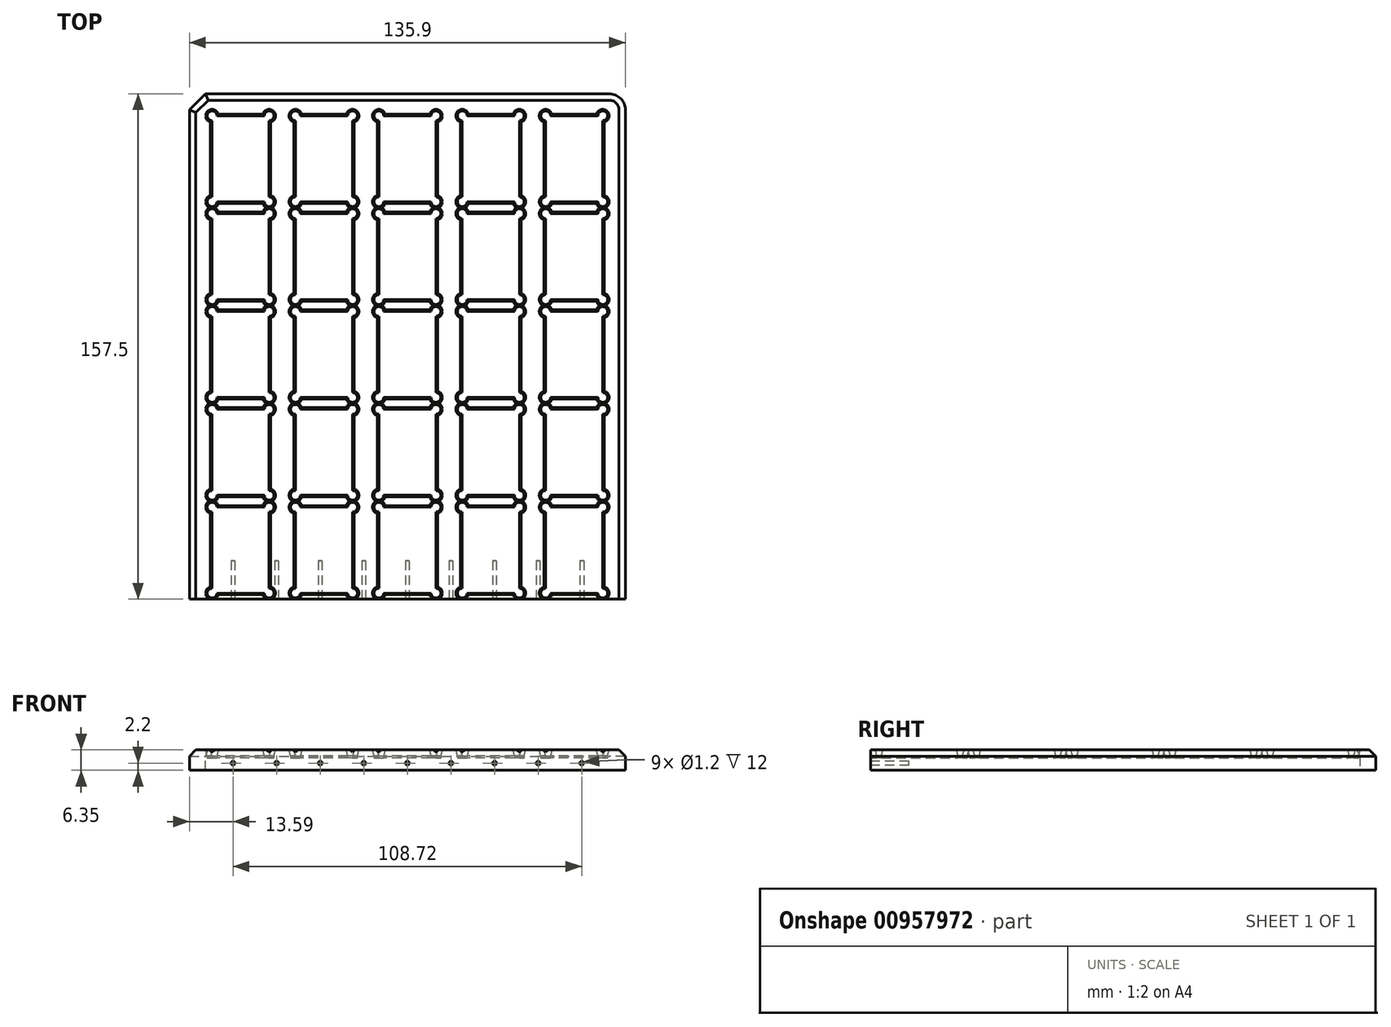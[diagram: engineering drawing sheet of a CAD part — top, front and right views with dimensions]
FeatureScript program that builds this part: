
annotation { "Feature Type Name" : "Feature", "Feature Type Description" : "" }
export const myFeature = defineFeature(function(context is Context, id is Id, definition is map)
    precondition{}
    {
        {
            var Q0;
            Q0=qCreatedBy(makeId("Top.planeOp"),FACE);
            var sketch = newSketch(context, id + "F0", { "sketchPlane" : qUnion([Q0])});
            skLineSegment(sketch, "E0.bottom", {"start": v(0, 0) * mm, "end": v(135.9, 0) * mm});
            skLineSegment(sketch, "E0.top", {"start": v(0, -157.5) * mm, "end": v(135.9, -157.5) * mm});
            skLineSegment(sketch, "E0.left", {"start": v(0, 0) * mm, "end": v(0, -157.5) * mm});
            skLineSegment(sketch, "E0.right", {"start": v(135.9, 0) * mm, "end": v(135.9, -157.5) * mm});
            skSolve(sketch);
        }
        {
            var Q0;
            Q0=makeQuery(id+"F0.imprint","IMPRINT",FACE,{"disambiguationData":[TD([[makeQuery(id+"F0.imprint","IMPRINT",EDGE,{"derivedFrom":sQuery(id+"F0.wireOp",EDGE,"E0.bottom")}),-1.0]])]});
            extrude(context, id + "F1", {"entities" : qUnion([Q0]), "depth" : 3.85 * mm, "offsetDistance" : 25 * mm});
        }
        {
            var Q0;
            Q0=makeQuery(id+"F1.opExtrude","SWEPT_EDGE",EDGE,{"disambiguationData":[OSD([sQuery(id+"F0.wireOp",EDGE,"E0.bottom"),sQuery(id+"F0.wireOp",EDGE,"E0.left")])]});
            chamfer(context, id + "F2", {"entities" : qUnion([Q0]), "chamferType" : ChamferType.OFFSET_ANGLE, "width" : 5 * mm, "oppositeDirection" : false, "angle" : 45 * degree, "tangentPropagation" : true});
        }
        {
            var Q0;
            {var subQ0=sQuery(id+"F0.wireOp",EDGE,"E0.right");var subQ1=sQuery(id+"F0.wireOp",EDGE,"E0.bottom");Q0=makeQuery(id+"F5.boolean.opBoolean","MERGE",EDGE,{"derivedFrom":[makeQuery(id+"F1.opExtrude","SWEPT_EDGE",EDGE,{"disambiguationData":[OSD([subQ1,subQ0])]}),makeQuery(id+"F5.opExtrude","SWEPT_EDGE",EDGE,{"disambiguationData":[OSD([subQ1,subQ0])]})]});}
            fillet(context, id + "F3", {"entities" : qUnion([Q0]), "radius" : 5 * mm, "tangentPropagation" : true, "allowEdgeOverflow" : false});
        }
        {
            var Q0;
            Q0=makeQuery(id+"F1.opExtrude","CAP_FACE",FACE,{"disambiguationData":[OSD([sQuery(id+"F0.wireOp",EDGE,"E0.bottom"),sQuery(id+"F0.wireOp",EDGE,"E0.top"),sQuery(id+"F0.wireOp",EDGE,"E0.left"),sQuery(id+"F0.wireOp",EDGE,"E0.right")])],"isStart":false});
            var sketch = newSketch(context, id + "F4", { "sketchPlane" : qUnion([Q0])});
            skLineSegment(sketch, "E1.bottom", {"start": v(24.85, -33.65) * mm, "end": v(7.05, -33.65) * mm});
            skLineSegment(sketch, "E1.top", {"start": v(24.85, -6.85) * mm, "end": v(7.05, -6.85) * mm});
            skLineSegment(sketch, "E1.left", {"start": v(24.85, -33.65) * mm, "end": v(24.85, -6.85) * mm});
            skLineSegment(sketch, "E1.right", {"start": v(7.05, -33.65) * mm, "end": v(7.05, -6.85) * mm});
            skPoint(sketch, "E1.middle", {"position": v(15.95, -20.25) * mm});
            skCircle(sketch, "E2", {"center": v(7.05, -6.85) * mm, "radius": 1.5 * mm});
            skCircle(sketch, "E3", {"center": v(24.85, -6.85) * mm, "radius": 1.5 * mm});
            skCircle(sketch, "E4", {"center": v(24.85, -33.65) * mm, "radius": 1.5 * mm});
            skCircle(sketch, "E5", {"center": v(7.05, -33.65) * mm, "radius": 1.5 * mm});
            skLineSegment(sketch, "E6.0.1.0", {"start": v(24.85, -64.15) * mm, "end": v(7.05, -64.15) * mm});
            skCircle(sketch, "E6.0.1.1", {"center": v(7.05, -64.15) * mm, "radius": 1.5 * mm});
            skLineSegment(sketch, "E6.0.1.2", {"start": v(7.05, -64.15) * mm, "end": v(7.05, -37.35) * mm});
            skCircle(sketch, "E6.0.1.3", {"center": v(7.05, -37.35) * mm, "radius": 1.5 * mm});
            skLineSegment(sketch, "E6.0.1.4", {"start": v(24.85, -37.35) * mm, "end": v(7.05, -37.35) * mm});
            skCircle(sketch, "E6.0.1.5", {"center": v(24.85, -37.35) * mm, "radius": 1.5 * mm});
            skLineSegment(sketch, "E6.0.1.6", {"start": v(24.85, -64.15) * mm, "end": v(24.85, -37.35) * mm});
            skCircle(sketch, "E6.0.1.7", {"center": v(24.85, -64.15) * mm, "radius": 1.5 * mm});
            skLineSegment(sketch, "E6.0.2.0", {"start": v(24.85, -94.65) * mm, "end": v(7.05, -94.65) * mm});
            skCircle(sketch, "E6.0.2.1", {"center": v(7.05, -94.65) * mm, "radius": 1.5 * mm});
            skLineSegment(sketch, "E6.0.2.2", {"start": v(7.05, -94.65) * mm, "end": v(7.05, -67.85) * mm});
            skCircle(sketch, "E6.0.2.3", {"center": v(7.05, -67.85) * mm, "radius": 1.5 * mm});
            skLineSegment(sketch, "E6.0.2.4", {"start": v(24.85, -67.85) * mm, "end": v(7.05, -67.85) * mm});
            skCircle(sketch, "E6.0.2.5", {"center": v(24.85, -67.85) * mm, "radius": 1.5 * mm});
            skLineSegment(sketch, "E6.0.2.6", {"start": v(24.85, -94.65) * mm, "end": v(24.85, -67.85) * mm});
            skCircle(sketch, "E6.0.2.7", {"center": v(24.85, -94.65) * mm, "radius": 1.5 * mm});
            skLineSegment(sketch, "E6.0.3.0", {"start": v(24.85, -125.15) * mm, "end": v(7.05, -125.15) * mm});
            skCircle(sketch, "E6.0.3.1", {"center": v(7.05, -125.15) * mm, "radius": 1.5 * mm});
            skLineSegment(sketch, "E6.0.3.2", {"start": v(7.05, -125.15) * mm, "end": v(7.05, -98.35) * mm});
            skCircle(sketch, "E6.0.3.3", {"center": v(7.05, -98.35) * mm, "radius": 1.5 * mm});
            skLineSegment(sketch, "E6.0.3.4", {"start": v(24.85, -98.35) * mm, "end": v(7.05, -98.35) * mm});
            skCircle(sketch, "E6.0.3.5", {"center": v(24.85, -98.35) * mm, "radius": 1.5 * mm});
            skLineSegment(sketch, "E6.0.3.6", {"start": v(24.85, -125.15) * mm, "end": v(24.85, -98.35) * mm});
            skCircle(sketch, "E6.0.3.7", {"center": v(24.85, -125.15) * mm, "radius": 1.5 * mm});
            skLineSegment(sketch, "E6.0.4.0", {"start": v(24.85, -155.65) * mm, "end": v(7.05, -155.65) * mm});
            skCircle(sketch, "E6.0.4.1", {"center": v(7.05, -155.65) * mm, "radius": 1.5 * mm});
            skLineSegment(sketch, "E6.0.4.2", {"start": v(7.05, -155.65) * mm, "end": v(7.05, -128.85) * mm});
            skCircle(sketch, "E6.0.4.3", {"center": v(7.05, -128.85) * mm, "radius": 1.5 * mm});
            skLineSegment(sketch, "E6.0.4.4", {"start": v(24.85, -128.85) * mm, "end": v(7.05, -128.85) * mm});
            skCircle(sketch, "E6.0.4.5", {"center": v(24.85, -128.85) * mm, "radius": 1.5 * mm});
            skLineSegment(sketch, "E6.0.4.6", {"start": v(24.85, -155.65) * mm, "end": v(24.85, -128.85) * mm});
            skCircle(sketch, "E6.0.4.7", {"center": v(24.85, -155.65) * mm, "radius": 1.5 * mm});
            skLineSegment(sketch, "E6.1.0.0", {"start": v(50.85, -33.65) * mm, "end": v(33.05, -33.65) * mm});
            skCircle(sketch, "E6.1.0.1", {"center": v(33.05, -33.65) * mm, "radius": 1.5 * mm});
            skLineSegment(sketch, "E6.1.0.2", {"start": v(33.05, -33.65) * mm, "end": v(33.05, -6.85) * mm});
            skCircle(sketch, "E6.1.0.3", {"center": v(33.05, -6.85) * mm, "radius": 1.5 * mm});
            skLineSegment(sketch, "E6.1.0.4", {"start": v(50.85, -6.85) * mm, "end": v(33.05, -6.85) * mm});
            skCircle(sketch, "E6.1.0.5", {"center": v(50.85, -6.85) * mm, "radius": 1.5 * mm});
            skLineSegment(sketch, "E6.1.0.6", {"start": v(50.85, -33.65) * mm, "end": v(50.85, -6.85) * mm});
            skCircle(sketch, "E6.1.0.7", {"center": v(50.85, -33.65) * mm, "radius": 1.5 * mm});
            skLineSegment(sketch, "E6.1.1.0", {"start": v(50.85, -64.15) * mm, "end": v(33.05, -64.15) * mm});
            skCircle(sketch, "E6.1.1.1", {"center": v(33.05, -64.15) * mm, "radius": 1.5 * mm});
            skLineSegment(sketch, "E6.1.1.2", {"start": v(33.05, -64.15) * mm, "end": v(33.05, -37.35) * mm});
            skCircle(sketch, "E6.1.1.3", {"center": v(33.05, -37.35) * mm, "radius": 1.5 * mm});
            skLineSegment(sketch, "E6.1.1.4", {"start": v(50.85, -37.35) * mm, "end": v(33.05, -37.35) * mm});
            skCircle(sketch, "E6.1.1.5", {"center": v(50.85, -37.35) * mm, "radius": 1.5 * mm});
            skLineSegment(sketch, "E6.1.1.6", {"start": v(50.85, -64.15) * mm, "end": v(50.85, -37.35) * mm});
            skCircle(sketch, "E6.1.1.7", {"center": v(50.85, -64.15) * mm, "radius": 1.5 * mm});
            skLineSegment(sketch, "E6.1.2.0", {"start": v(50.85, -94.65) * mm, "end": v(33.05, -94.65) * mm});
            skCircle(sketch, "E6.1.2.1", {"center": v(33.05, -94.65) * mm, "radius": 1.5 * mm});
            skLineSegment(sketch, "E6.1.2.2", {"start": v(33.05, -94.65) * mm, "end": v(33.05, -67.85) * mm});
            skCircle(sketch, "E6.1.2.3", {"center": v(33.05, -67.85) * mm, "radius": 1.5 * mm});
            skLineSegment(sketch, "E6.1.2.4", {"start": v(50.85, -67.85) * mm, "end": v(33.05, -67.85) * mm});
            skCircle(sketch, "E6.1.2.5", {"center": v(50.85, -67.85) * mm, "radius": 1.5 * mm});
            skLineSegment(sketch, "E6.1.2.6", {"start": v(50.85, -94.65) * mm, "end": v(50.85, -67.85) * mm});
            skCircle(sketch, "E6.1.2.7", {"center": v(50.85, -94.65) * mm, "radius": 1.5 * mm});
            skLineSegment(sketch, "E6.1.3.0", {"start": v(50.85, -125.15) * mm, "end": v(33.05, -125.15) * mm});
            skCircle(sketch, "E6.1.3.1", {"center": v(33.05, -125.15) * mm, "radius": 1.5 * mm});
            skLineSegment(sketch, "E6.1.3.2", {"start": v(33.05, -125.15) * mm, "end": v(33.05, -98.35) * mm});
            skCircle(sketch, "E6.1.3.3", {"center": v(33.05, -98.35) * mm, "radius": 1.5 * mm});
            skLineSegment(sketch, "E6.1.3.4", {"start": v(50.85, -98.35) * mm, "end": v(33.05, -98.35) * mm});
            skCircle(sketch, "E6.1.3.5", {"center": v(50.85, -98.35) * mm, "radius": 1.5 * mm});
            skLineSegment(sketch, "E6.1.3.6", {"start": v(50.85, -125.15) * mm, "end": v(50.85, -98.35) * mm});
            skCircle(sketch, "E6.1.3.7", {"center": v(50.85, -125.15) * mm, "radius": 1.5 * mm});
            skLineSegment(sketch, "E6.1.4.0", {"start": v(50.85, -155.65) * mm, "end": v(33.05, -155.65) * mm});
            skCircle(sketch, "E6.1.4.1", {"center": v(33.05, -155.65) * mm, "radius": 1.5 * mm});
            skLineSegment(sketch, "E6.1.4.2", {"start": v(33.05, -155.65) * mm, "end": v(33.05, -128.85) * mm});
            skCircle(sketch, "E6.1.4.3", {"center": v(33.05, -128.85) * mm, "radius": 1.5 * mm});
            skLineSegment(sketch, "E6.1.4.4", {"start": v(50.85, -128.85) * mm, "end": v(33.05, -128.85) * mm});
            skCircle(sketch, "E6.1.4.5", {"center": v(50.85, -128.85) * mm, "radius": 1.5 * mm});
            skLineSegment(sketch, "E6.1.4.6", {"start": v(50.85, -155.65) * mm, "end": v(50.85, -128.85) * mm});
            skCircle(sketch, "E6.1.4.7", {"center": v(50.85, -155.65) * mm, "radius": 1.5 * mm});
            skLineSegment(sketch, "E6.2.0.0", {"start": v(76.85, -33.65) * mm, "end": v(59.05, -33.65) * mm});
            skCircle(sketch, "E6.2.0.1", {"center": v(59.05, -33.65) * mm, "radius": 1.5 * mm});
            skLineSegment(sketch, "E6.2.0.2", {"start": v(59.05, -33.65) * mm, "end": v(59.05, -6.85) * mm});
            skCircle(sketch, "E6.2.0.3", {"center": v(59.05, -6.85) * mm, "radius": 1.5 * mm});
            skLineSegment(sketch, "E6.2.0.4", {"start": v(76.85, -6.85) * mm, "end": v(59.05, -6.85) * mm});
            skCircle(sketch, "E6.2.0.5", {"center": v(76.85, -6.85) * mm, "radius": 1.5 * mm});
            skLineSegment(sketch, "E6.2.0.6", {"start": v(76.85, -33.65) * mm, "end": v(76.85, -6.85) * mm});
            skCircle(sketch, "E6.2.0.7", {"center": v(76.85, -33.65) * mm, "radius": 1.5 * mm});
            skLineSegment(sketch, "E6.2.1.0", {"start": v(76.85, -64.15) * mm, "end": v(59.05, -64.15) * mm});
            skCircle(sketch, "E6.2.1.1", {"center": v(59.05, -64.15) * mm, "radius": 1.5 * mm});
            skLineSegment(sketch, "E6.2.1.2", {"start": v(59.05, -64.15) * mm, "end": v(59.05, -37.35) * mm});
            skCircle(sketch, "E6.2.1.3", {"center": v(59.05, -37.35) * mm, "radius": 1.5 * mm});
            skLineSegment(sketch, "E6.2.1.4", {"start": v(76.85, -37.35) * mm, "end": v(59.05, -37.35) * mm});
            skCircle(sketch, "E6.2.1.5", {"center": v(76.85, -37.35) * mm, "radius": 1.5 * mm});
            skLineSegment(sketch, "E6.2.1.6", {"start": v(76.85, -64.15) * mm, "end": v(76.85, -37.35) * mm});
            skCircle(sketch, "E6.2.1.7", {"center": v(76.85, -64.15) * mm, "radius": 1.5 * mm});
            skLineSegment(sketch, "E6.2.2.0", {"start": v(76.85, -94.65) * mm, "end": v(59.05, -94.65) * mm});
            skCircle(sketch, "E6.2.2.1", {"center": v(59.05, -94.65) * mm, "radius": 1.5 * mm});
            skLineSegment(sketch, "E6.2.2.2", {"start": v(59.05, -94.65) * mm, "end": v(59.05, -67.85) * mm});
            skCircle(sketch, "E6.2.2.3", {"center": v(59.05, -67.85) * mm, "radius": 1.5 * mm});
            skLineSegment(sketch, "E6.2.2.4", {"start": v(76.85, -67.85) * mm, "end": v(59.05, -67.85) * mm});
            skCircle(sketch, "E6.2.2.5", {"center": v(76.85, -67.85) * mm, "radius": 1.5 * mm});
            skLineSegment(sketch, "E6.2.2.6", {"start": v(76.85, -94.65) * mm, "end": v(76.85, -67.85) * mm});
            skCircle(sketch, "E6.2.2.7", {"center": v(76.85, -94.65) * mm, "radius": 1.5 * mm});
            skLineSegment(sketch, "E6.2.3.0", {"start": v(76.85, -125.15) * mm, "end": v(59.05, -125.15) * mm});
            skCircle(sketch, "E6.2.3.1", {"center": v(59.05, -125.15) * mm, "radius": 1.5 * mm});
            skLineSegment(sketch, "E6.2.3.2", {"start": v(59.05, -125.15) * mm, "end": v(59.05, -98.35) * mm});
            skCircle(sketch, "E6.2.3.3", {"center": v(59.05, -98.35) * mm, "radius": 1.5 * mm});
            skLineSegment(sketch, "E6.2.3.4", {"start": v(76.85, -98.35) * mm, "end": v(59.05, -98.35) * mm});
            skCircle(sketch, "E6.2.3.5", {"center": v(76.85, -98.35) * mm, "radius": 1.5 * mm});
            skLineSegment(sketch, "E6.2.3.6", {"start": v(76.85, -125.15) * mm, "end": v(76.85, -98.35) * mm});
            skCircle(sketch, "E6.2.3.7", {"center": v(76.85, -125.15) * mm, "radius": 1.5 * mm});
            skLineSegment(sketch, "E6.2.4.0", {"start": v(76.85, -155.65) * mm, "end": v(59.05, -155.65) * mm});
            skCircle(sketch, "E6.2.4.1", {"center": v(59.05, -155.65) * mm, "radius": 1.5 * mm});
            skLineSegment(sketch, "E6.2.4.2", {"start": v(59.05, -155.65) * mm, "end": v(59.05, -128.85) * mm});
            skCircle(sketch, "E6.2.4.3", {"center": v(59.05, -128.85) * mm, "radius": 1.5 * mm});
            skLineSegment(sketch, "E6.2.4.4", {"start": v(76.85, -128.85) * mm, "end": v(59.05, -128.85) * mm});
            skCircle(sketch, "E6.2.4.5", {"center": v(76.85, -128.85) * mm, "radius": 1.5 * mm});
            skLineSegment(sketch, "E6.2.4.6", {"start": v(76.85, -155.65) * mm, "end": v(76.85, -128.85) * mm});
            skCircle(sketch, "E6.2.4.7", {"center": v(76.85, -155.65) * mm, "radius": 1.5 * mm});
            skLineSegment(sketch, "E6.3.0.0", {"start": v(102.85, -33.65) * mm, "end": v(85.05, -33.65) * mm});
            skCircle(sketch, "E6.3.0.1", {"center": v(85.05, -33.65) * mm, "radius": 1.5 * mm});
            skLineSegment(sketch, "E6.3.0.2", {"start": v(85.05, -33.65) * mm, "end": v(85.05, -6.85) * mm});
            skCircle(sketch, "E6.3.0.3", {"center": v(85.05, -6.85) * mm, "radius": 1.5 * mm});
            skLineSegment(sketch, "E6.3.0.4", {"start": v(102.85, -6.85) * mm, "end": v(85.05, -6.85) * mm});
            skCircle(sketch, "E6.3.0.5", {"center": v(102.85, -6.85) * mm, "radius": 1.5 * mm});
            skLineSegment(sketch, "E6.3.0.6", {"start": v(102.85, -33.65) * mm, "end": v(102.85, -6.85) * mm});
            skCircle(sketch, "E6.3.0.7", {"center": v(102.85, -33.65) * mm, "radius": 1.5 * mm});
            skLineSegment(sketch, "E6.3.1.0", {"start": v(102.85, -64.15) * mm, "end": v(85.05, -64.15) * mm});
            skCircle(sketch, "E6.3.1.1", {"center": v(85.05, -64.15) * mm, "radius": 1.5 * mm});
            skLineSegment(sketch, "E6.3.1.2", {"start": v(85.05, -64.15) * mm, "end": v(85.05, -37.35) * mm});
            skCircle(sketch, "E6.3.1.3", {"center": v(85.05, -37.35) * mm, "radius": 1.5 * mm});
            skLineSegment(sketch, "E6.3.1.4", {"start": v(102.85, -37.35) * mm, "end": v(85.05, -37.35) * mm});
            skCircle(sketch, "E6.3.1.5", {"center": v(102.85, -37.35) * mm, "radius": 1.5 * mm});
            skLineSegment(sketch, "E6.3.1.6", {"start": v(102.85, -64.15) * mm, "end": v(102.85, -37.35) * mm});
            skCircle(sketch, "E6.3.1.7", {"center": v(102.85, -64.15) * mm, "radius": 1.5 * mm});
            skLineSegment(sketch, "E6.3.2.0", {"start": v(102.85, -94.65) * mm, "end": v(85.05, -94.65) * mm});
            skCircle(sketch, "E6.3.2.1", {"center": v(85.05, -94.65) * mm, "radius": 1.5 * mm});
            skLineSegment(sketch, "E6.3.2.2", {"start": v(85.05, -94.65) * mm, "end": v(85.05, -67.85) * mm});
            skCircle(sketch, "E6.3.2.3", {"center": v(85.05, -67.85) * mm, "radius": 1.5 * mm});
            skLineSegment(sketch, "E6.3.2.4", {"start": v(102.85, -67.85) * mm, "end": v(85.05, -67.85) * mm});
            skCircle(sketch, "E6.3.2.5", {"center": v(102.85, -67.85) * mm, "radius": 1.5 * mm});
            skLineSegment(sketch, "E6.3.2.6", {"start": v(102.85, -94.65) * mm, "end": v(102.85, -67.85) * mm});
            skCircle(sketch, "E6.3.2.7", {"center": v(102.85, -94.65) * mm, "radius": 1.5 * mm});
            skLineSegment(sketch, "E6.3.3.0", {"start": v(102.85, -125.15) * mm, "end": v(85.05, -125.15) * mm});
            skCircle(sketch, "E6.3.3.1", {"center": v(85.05, -125.15) * mm, "radius": 1.5 * mm});
            skLineSegment(sketch, "E6.3.3.2", {"start": v(85.05, -125.15) * mm, "end": v(85.05, -98.35) * mm});
            skCircle(sketch, "E6.3.3.3", {"center": v(85.05, -98.35) * mm, "radius": 1.5 * mm});
            skLineSegment(sketch, "E6.3.3.4", {"start": v(102.85, -98.35) * mm, "end": v(85.05, -98.35) * mm});
            skCircle(sketch, "E6.3.3.5", {"center": v(102.85, -98.35) * mm, "radius": 1.5 * mm});
            skLineSegment(sketch, "E6.3.3.6", {"start": v(102.85, -125.15) * mm, "end": v(102.85, -98.35) * mm});
            skCircle(sketch, "E6.3.3.7", {"center": v(102.85, -125.15) * mm, "radius": 1.5 * mm});
            skLineSegment(sketch, "E6.3.4.0", {"start": v(102.85, -155.65) * mm, "end": v(85.05, -155.65) * mm});
            skCircle(sketch, "E6.3.4.1", {"center": v(85.05, -155.65) * mm, "radius": 1.5 * mm});
            skLineSegment(sketch, "E6.3.4.2", {"start": v(85.05, -155.65) * mm, "end": v(85.05, -128.85) * mm});
            skCircle(sketch, "E6.3.4.3", {"center": v(85.05, -128.85) * mm, "radius": 1.5 * mm});
            skLineSegment(sketch, "E6.3.4.4", {"start": v(102.85, -128.85) * mm, "end": v(85.05, -128.85) * mm});
            skCircle(sketch, "E6.3.4.5", {"center": v(102.85, -128.85) * mm, "radius": 1.5 * mm});
            skLineSegment(sketch, "E6.3.4.6", {"start": v(102.85, -155.65) * mm, "end": v(102.85, -128.85) * mm});
            skCircle(sketch, "E6.3.4.7", {"center": v(102.85, -155.65) * mm, "radius": 1.5 * mm});
            skLineSegment(sketch, "E6.4.0.0", {"start": v(128.85, -33.65) * mm, "end": v(111.05, -33.65) * mm});
            skCircle(sketch, "E6.4.0.1", {"center": v(111.05, -33.65) * mm, "radius": 1.5 * mm});
            skLineSegment(sketch, "E6.4.0.2", {"start": v(111.05, -33.65) * mm, "end": v(111.05, -6.85) * mm});
            skCircle(sketch, "E6.4.0.3", {"center": v(111.05, -6.85) * mm, "radius": 1.5 * mm});
            skLineSegment(sketch, "E6.4.0.4", {"start": v(128.85, -6.85) * mm, "end": v(111.05, -6.85) * mm});
            skCircle(sketch, "E6.4.0.5", {"center": v(128.85, -6.85) * mm, "radius": 1.5 * mm});
            skLineSegment(sketch, "E6.4.0.6", {"start": v(128.85, -33.65) * mm, "end": v(128.85, -6.85) * mm});
            skCircle(sketch, "E6.4.0.7", {"center": v(128.85, -33.65) * mm, "radius": 1.5 * mm});
            skLineSegment(sketch, "E6.4.1.0", {"start": v(128.85, -64.15) * mm, "end": v(111.05, -64.15) * mm});
            skCircle(sketch, "E6.4.1.1", {"center": v(111.05, -64.15) * mm, "radius": 1.5 * mm});
            skLineSegment(sketch, "E6.4.1.2", {"start": v(111.05, -64.15) * mm, "end": v(111.05, -37.35) * mm});
            skCircle(sketch, "E6.4.1.3", {"center": v(111.05, -37.35) * mm, "radius": 1.5 * mm});
            skLineSegment(sketch, "E6.4.1.4", {"start": v(128.85, -37.35) * mm, "end": v(111.05, -37.35) * mm});
            skCircle(sketch, "E6.4.1.5", {"center": v(128.85, -37.35) * mm, "radius": 1.5 * mm});
            skLineSegment(sketch, "E6.4.1.6", {"start": v(128.85, -64.15) * mm, "end": v(128.85, -37.35) * mm});
            skCircle(sketch, "E6.4.1.7", {"center": v(128.85, -64.15) * mm, "radius": 1.5 * mm});
            skLineSegment(sketch, "E6.4.2.0", {"start": v(128.85, -94.65) * mm, "end": v(111.05, -94.65) * mm});
            skCircle(sketch, "E6.4.2.1", {"center": v(111.05, -94.65) * mm, "radius": 1.5 * mm});
            skLineSegment(sketch, "E6.4.2.2", {"start": v(111.05, -94.65) * mm, "end": v(111.05, -67.85) * mm});
            skCircle(sketch, "E6.4.2.3", {"center": v(111.05, -67.85) * mm, "radius": 1.5 * mm});
            skLineSegment(sketch, "E6.4.2.4", {"start": v(128.85, -67.85) * mm, "end": v(111.05, -67.85) * mm});
            skCircle(sketch, "E6.4.2.5", {"center": v(128.85, -67.85) * mm, "radius": 1.5 * mm});
            skLineSegment(sketch, "E6.4.2.6", {"start": v(128.85, -94.65) * mm, "end": v(128.85, -67.85) * mm});
            skCircle(sketch, "E6.4.2.7", {"center": v(128.85, -94.65) * mm, "radius": 1.5 * mm});
            skLineSegment(sketch, "E6.4.3.0", {"start": v(128.85, -125.15) * mm, "end": v(111.05, -125.15) * mm});
            skCircle(sketch, "E6.4.3.1", {"center": v(111.05, -125.15) * mm, "radius": 1.5 * mm});
            skLineSegment(sketch, "E6.4.3.2", {"start": v(111.05, -125.15) * mm, "end": v(111.05, -98.35) * mm});
            skCircle(sketch, "E6.4.3.3", {"center": v(111.05, -98.35) * mm, "radius": 1.5 * mm});
            skLineSegment(sketch, "E6.4.3.4", {"start": v(128.85, -98.35) * mm, "end": v(111.05, -98.35) * mm});
            skCircle(sketch, "E6.4.3.5", {"center": v(128.85, -98.35) * mm, "radius": 1.5 * mm});
            skLineSegment(sketch, "E6.4.3.6", {"start": v(128.85, -125.15) * mm, "end": v(128.85, -98.35) * mm});
            skCircle(sketch, "E6.4.3.7", {"center": v(128.85, -125.15) * mm, "radius": 1.5 * mm});
            skLineSegment(sketch, "E6.4.4.0", {"start": v(128.85, -155.65) * mm, "end": v(111.05, -155.65) * mm});
            skCircle(sketch, "E6.4.4.1", {"center": v(111.05, -155.65) * mm, "radius": 1.5 * mm});
            skLineSegment(sketch, "E6.4.4.2", {"start": v(111.05, -155.65) * mm, "end": v(111.05, -128.85) * mm});
            skCircle(sketch, "E6.4.4.3", {"center": v(111.05, -128.85) * mm, "radius": 1.5 * mm});
            skLineSegment(sketch, "E6.4.4.4", {"start": v(128.85, -128.85) * mm, "end": v(111.05, -128.85) * mm});
            skCircle(sketch, "E6.4.4.5", {"center": v(128.85, -128.85) * mm, "radius": 1.5 * mm});
            skLineSegment(sketch, "E6.4.4.6", {"start": v(128.85, -155.65) * mm, "end": v(128.85, -128.85) * mm});
            skCircle(sketch, "E6.4.4.7", {"center": v(128.85, -155.65) * mm, "radius": 1.5 * mm});
            skLineSegment(sketch, "E6.direction1", {"start": v(7.05, -33.65) * mm, "end": v(33.05, -33.65) * mm, "construction": true});
            skLineSegment(sketch, "E6.direction2", {"start": v(7.05, -33.65) * mm, "end": v(7.05, -64.15) * mm, "construction": true});
            skSolve(sketch);
        }
        {
            var Q0;
            {var subQ603=sQuery(id+"F0.wireOp",EDGE,"E0.top");Q0=makeQuery(id+"F4.imprint","IMPRINT",FACE,{"disambiguationData":[TD([[makeQuery(id+"F4.imprint","IMPRINT",EDGE,{"derivedFrom":makeQuery(id+"F1.opExtrude","CAP_EDGE",EDGE,{"disambiguationData":[OSD([subQ603])],"isStart":false})}),1.0]])]});}
            extrude(context, id + "F5", {"entities" : qUnion([Q0]), "operationType" : NewBodyOperationType.ADD, "depth" : 2.5 * mm, "offsetDistance" : 25 * mm});
        }
        {
            var Q0;
            {var subQ0=sQuery(id+"F0.wireOp",EDGE,"E0.top");Q0=makeQuery(id+"F5.boolean.opBoolean","MERGE",FACE,{"derivedFrom":[makeQuery(id+"F1.opExtrude","SWEPT_FACE",FACE,{"disambiguationData":[OSD([subQ0])]}),makeQuery(id+"F5.opExtrude","SWEPT_FACE",FACE,{"disambiguationData":[OSD([subQ0])]})]});}
            var sketch = newSketch(context, id + "F6", { "sketchPlane" : qUnion([Q0])});
            skCircle(sketch, "E7", {"center": v(13.6, 2.2) * mm, "radius": 0.6 * mm});
            skCircle(sketch, "E8.1.0.0", {"center": v(27.18, 2.2) * mm, "radius": 0.6 * mm});
            skCircle(sketch, "E8.2.0.0", {"center": v(40.77, 2.2) * mm, "radius": 0.6 * mm});
            skCircle(sketch, "E8.3.0.0", {"center": v(54.36, 2.2) * mm, "radius": 0.6 * mm});
            skCircle(sketch, "E8.4.0.0", {"center": v(67.95, 2.2) * mm, "radius": 0.6 * mm});
            skCircle(sketch, "E8.5.0.0", {"center": v(81.54, 2.2) * mm, "radius": 0.6 * mm});
            skCircle(sketch, "E8.6.0.0", {"center": v(95.13, 2.2) * mm, "radius": 0.6 * mm});
            skCircle(sketch, "E8.7.0.0", {"center": v(108.72, 2.2) * mm, "radius": 0.6 * mm});
            skCircle(sketch, "E8.8.0.0", {"center": v(122.31, 2.2) * mm, "radius": 0.6 * mm});
            skLineSegment(sketch, "E8.direction1", {"start": v(27.18, 2.2) * mm, "end": v(40.77, 2.2) * mm, "construction": true});
            skSolve(sketch);
        }
        {
            var Q0;
            Q0=makeQuery(id+"F6.imprint","IMPRINT",FACE,{"disambiguationData":[TD([[makeQuery(id+"F6.imprint","IMPRINT",EDGE,{"derivedFrom":sQuery(id+"F6.wireOp",EDGE,"E7")}),1.0]])]});
            var Q1;
            Q1=makeQuery(id+"F6.imprint","IMPRINT",FACE,{"disambiguationData":[TD([[makeQuery(id+"F6.imprint","IMPRINT",EDGE,{"derivedFrom":sQuery(id+"F6.wireOp",EDGE,"E8.1.0.0")}),1.0]])]});
            var Q2;
            Q2=makeQuery(id+"F6.imprint","IMPRINT",FACE,{"disambiguationData":[TD([[makeQuery(id+"F6.imprint","IMPRINT",EDGE,{"derivedFrom":sQuery(id+"F6.wireOp",EDGE,"E8.2.0.0")}),1.0]])]});
            var Q3;
            Q3=makeQuery(id+"F6.imprint","IMPRINT",FACE,{"disambiguationData":[TD([[makeQuery(id+"F6.imprint","IMPRINT",EDGE,{"derivedFrom":sQuery(id+"F6.wireOp",EDGE,"E8.3.0.0")}),1.0]])]});
            var Q4;
            Q4=makeQuery(id+"F6.imprint","IMPRINT",FACE,{"disambiguationData":[TD([[makeQuery(id+"F6.imprint","IMPRINT",EDGE,{"derivedFrom":sQuery(id+"F6.wireOp",EDGE,"E8.4.0.0")}),1.0]])]});
            var Q5;
            Q5=makeQuery(id+"F6.imprint","IMPRINT",FACE,{"disambiguationData":[TD([[makeQuery(id+"F6.imprint","IMPRINT",EDGE,{"derivedFrom":sQuery(id+"F6.wireOp",EDGE,"E8.5.0.0")}),1.0]])]});
            var Q6;
            Q6=makeQuery(id+"F6.imprint","IMPRINT",FACE,{"disambiguationData":[TD([[makeQuery(id+"F6.imprint","IMPRINT",EDGE,{"derivedFrom":sQuery(id+"F6.wireOp",EDGE,"E8.6.0.0")}),1.0]])]});
            var Q7;
            Q7=makeQuery(id+"F6.imprint","IMPRINT",FACE,{"disambiguationData":[TD([[makeQuery(id+"F6.imprint","IMPRINT",EDGE,{"derivedFrom":sQuery(id+"F6.wireOp",EDGE,"E8.7.0.0")}),1.0]])]});
            var Q8;
            Q8=makeQuery(id+"F6.imprint","IMPRINT",FACE,{"disambiguationData":[TD([[makeQuery(id+"F6.imprint","IMPRINT",EDGE,{"derivedFrom":sQuery(id+"F6.wireOp",EDGE,"E8.8.0.0")}),1.0]])]});
            var Q9;
            Q9=sQuery(id+"F6.wireOp",EDGE,"E7");
            var Q10;
            Q10=sQuery(id+"F6.wireOp",EDGE,"E8.1.0.0");
            var Q11;
            Q11=sQuery(id+"F6.wireOp",EDGE,"E8.2.0.0");
            var Q12;
            Q12=sQuery(id+"F6.wireOp",EDGE,"E8.3.0.0");
            var Q13;
            Q13=sQuery(id+"F6.wireOp",EDGE,"E8.4.0.0");
            var Q14;
            Q14=sQuery(id+"F6.wireOp",EDGE,"E8.5.0.0");
            extrude(context, id + "F7", {"entities" : qUnion([Q0, Q1, Q2, Q3, Q4, Q5, Q6, Q7, Q8]), "operationType" : NewBodyOperationType.REMOVE, "surfaceEntities" : qUnion([Q9, Q10, Q11, Q12, Q13, Q14]), "oppositeDirection" : true, "depth" : 12 * mm, "offsetDistance" : 25 * mm});
        }
        {
            var Q0;
            Q0=makeQuery(id+"F5.opExtrude","CAP_EDGE",EDGE,{"disambiguationData":[OSD([sQuery(id+"F4.wireOp",EDGE,"E1.right")])],"isStart":false});
            var Q1;
            Q1=makeQuery(id+"F5.opExtrude","CAP_EDGE",EDGE,{"disambiguationData":[OSD([sQuery(id+"F4.wireOp",EDGE,"E1.left")])],"isStart":false});
            var Q2;
            Q2=makeQuery(id+"F5.opExtrude","CAP_EDGE",EDGE,{"disambiguationData":[OSD([sQuery(id+"F4.wireOp",EDGE,"E6.1.0.2")])],"isStart":false});
            var Q3;
            Q3=makeQuery(id+"F5.opExtrude","CAP_EDGE",EDGE,{"disambiguationData":[OSD([sQuery(id+"F4.wireOp",EDGE,"E6.1.0.6")])],"isStart":false});
            var Q4;
            Q4=makeQuery(id+"F5.opExtrude","CAP_EDGE",EDGE,{"disambiguationData":[OSD([sQuery(id+"F4.wireOp",EDGE,"E6.2.0.2")])],"isStart":false});
            var Q5;
            Q5=makeQuery(id+"F5.opExtrude","CAP_EDGE",EDGE,{"disambiguationData":[OSD([sQuery(id+"F4.wireOp",EDGE,"E6.2.0.6")])],"isStart":false});
            var Q6;
            Q6=makeQuery(id+"F5.opExtrude","CAP_EDGE",EDGE,{"disambiguationData":[OSD([sQuery(id+"F4.wireOp",EDGE,"E6.3.0.2")])],"isStart":false});
            var Q7;
            Q7=makeQuery(id+"F5.opExtrude","CAP_EDGE",EDGE,{"disambiguationData":[OSD([sQuery(id+"F4.wireOp",EDGE,"E6.3.0.6")])],"isStart":false});
            var Q8;
            Q8=makeQuery(id+"F5.opExtrude","CAP_EDGE",EDGE,{"disambiguationData":[OSD([sQuery(id+"F4.wireOp",EDGE,"E6.4.0.2")])],"isStart":false});
            var Q9;
            Q9=makeQuery(id+"F5.opExtrude","CAP_EDGE",EDGE,{"disambiguationData":[OSD([sQuery(id+"F4.wireOp",EDGE,"E6.4.0.6")])],"isStart":false});
            var Q10;
            Q10=makeQuery(id+"F5.opExtrude","CAP_EDGE",EDGE,{"disambiguationData":[OSD([sQuery(id+"F4.wireOp",EDGE,"E1.top")])],"isStart":false});
            var Q11;
            Q11=makeQuery(id+"F5.opExtrude","CAP_EDGE",EDGE,{"disambiguationData":[OSD([sQuery(id+"F4.wireOp",EDGE,"E1.bottom")])],"isStart":false});
            var Q12;
            Q12=makeQuery(id+"F5.opExtrude","CAP_EDGE",EDGE,{"disambiguationData":[OSD([sQuery(id+"F4.wireOp",EDGE,"E6.1.0.0")])],"isStart":false});
            var Q13;
            Q13=makeQuery(id+"F5.opExtrude","CAP_EDGE",EDGE,{"disambiguationData":[OSD([sQuery(id+"F4.wireOp",EDGE,"E6.1.0.4")])],"isStart":false});
            var Q14;
            Q14=makeQuery(id+"F5.opExtrude","CAP_EDGE",EDGE,{"disambiguationData":[OSD([sQuery(id+"F4.wireOp",EDGE,"E6.2.0.0")])],"isStart":false});
            var Q15;
            Q15=makeQuery(id+"F5.opExtrude","CAP_EDGE",EDGE,{"disambiguationData":[OSD([sQuery(id+"F4.wireOp",EDGE,"E6.2.0.4")])],"isStart":false});
            var Q16;
            Q16=makeQuery(id+"F5.opExtrude","CAP_EDGE",EDGE,{"disambiguationData":[OSD([sQuery(id+"F4.wireOp",EDGE,"E6.3.0.4")])],"isStart":false});
            var Q17;
            Q17=makeQuery(id+"F5.opExtrude","CAP_EDGE",EDGE,{"disambiguationData":[OSD([sQuery(id+"F4.wireOp",EDGE,"E6.3.0.0")])],"isStart":false});
            var Q18;
            Q18=makeQuery(id+"F5.opExtrude","CAP_EDGE",EDGE,{"disambiguationData":[OSD([sQuery(id+"F4.wireOp",EDGE,"E6.4.0.0")])],"isStart":false});
            var Q19;
            Q19=makeQuery(id+"F5.opExtrude","CAP_EDGE",EDGE,{"disambiguationData":[OSD([sQuery(id+"F4.wireOp",EDGE,"E6.4.0.4")])],"isStart":false});
            var Q20;
            Q20=makeQuery(id+"F5.opExtrude","CAP_EDGE",EDGE,{"disambiguationData":[OSD([sQuery(id+"F4.wireOp",EDGE,"E6.4.1.2")])],"isStart":false});
            var Q21;
            Q21=makeQuery(id+"F5.opExtrude","CAP_EDGE",EDGE,{"disambiguationData":[OSD([sQuery(id+"F4.wireOp",EDGE,"E6.4.1.6")])],"isStart":false});
            var Q22;
            Q22=makeQuery(id+"F5.opExtrude","CAP_EDGE",EDGE,{"disambiguationData":[OSD([sQuery(id+"F4.wireOp",EDGE,"E6.4.1.4")])],"isStart":false});
            var Q23;
            Q23=makeQuery(id+"F5.opExtrude","CAP_EDGE",EDGE,{"disambiguationData":[OSD([sQuery(id+"F4.wireOp",EDGE,"E6.4.1.0")])],"isStart":false});
            var Q24;
            Q24=makeQuery(id+"F5.opExtrude","CAP_EDGE",EDGE,{"disambiguationData":[OSD([sQuery(id+"F4.wireOp",EDGE,"E6.3.1.0")])],"isStart":false});
            var Q25;
            Q25=makeQuery(id+"F5.opExtrude","CAP_EDGE",EDGE,{"disambiguationData":[OSD([sQuery(id+"F4.wireOp",EDGE,"E6.3.1.4")])],"isStart":false});
            var Q26;
            Q26=makeQuery(id+"F5.opExtrude","CAP_EDGE",EDGE,{"disambiguationData":[OSD([sQuery(id+"F4.wireOp",EDGE,"E6.3.1.6")])],"isStart":false});
            var Q27;
            Q27=makeQuery(id+"F5.opExtrude","CAP_EDGE",EDGE,{"disambiguationData":[OSD([sQuery(id+"F4.wireOp",EDGE,"E6.3.1.2")])],"isStart":false});
            var Q28;
            Q28=makeQuery(id+"F5.opExtrude","CAP_EDGE",EDGE,{"disambiguationData":[OSD([sQuery(id+"F4.wireOp",EDGE,"E6.2.1.6")])],"isStart":false});
            var Q29;
            Q29=makeQuery(id+"F5.opExtrude","CAP_EDGE",EDGE,{"disambiguationData":[OSD([sQuery(id+"F4.wireOp",EDGE,"E6.2.1.4")])],"isStart":false});
            var Q30;
            Q30=makeQuery(id+"F5.opExtrude","CAP_EDGE",EDGE,{"disambiguationData":[OSD([sQuery(id+"F4.wireOp",EDGE,"E6.2.1.0")])],"isStart":false});
            var Q31;
            Q31=makeQuery(id+"F5.opExtrude","CAP_EDGE",EDGE,{"disambiguationData":[OSD([sQuery(id+"F4.wireOp",EDGE,"E6.2.1.2")])],"isStart":false});
            var Q32;
            Q32=makeQuery(id+"F5.opExtrude","CAP_EDGE",EDGE,{"disambiguationData":[OSD([sQuery(id+"F4.wireOp",EDGE,"E6.1.1.6")])],"isStart":false});
            var Q33;
            Q33=makeQuery(id+"F5.opExtrude","CAP_EDGE",EDGE,{"disambiguationData":[OSD([sQuery(id+"F4.wireOp",EDGE,"E6.1.1.4")])],"isStart":false});
            var Q34;
            Q34=makeQuery(id+"F5.opExtrude","CAP_EDGE",EDGE,{"disambiguationData":[OSD([sQuery(id+"F4.wireOp",EDGE,"E6.1.1.0")])],"isStart":false});
            var Q35;
            Q35=makeQuery(id+"F5.opExtrude","CAP_EDGE",EDGE,{"disambiguationData":[OSD([sQuery(id+"F4.wireOp",EDGE,"E6.1.1.2")])],"isStart":false});
            var Q36;
            Q36=makeQuery(id+"F5.opExtrude","CAP_EDGE",EDGE,{"disambiguationData":[OSD([sQuery(id+"F4.wireOp",EDGE,"E6.0.1.6")])],"isStart":false});
            var Q37;
            Q37=makeQuery(id+"F5.opExtrude","CAP_EDGE",EDGE,{"disambiguationData":[OSD([sQuery(id+"F4.wireOp",EDGE,"E6.0.1.2")])],"isStart":false});
            var Q38;
            Q38=makeQuery(id+"F5.opExtrude","CAP_EDGE",EDGE,{"disambiguationData":[OSD([sQuery(id+"F4.wireOp",EDGE,"E6.0.1.4")])],"isStart":false});
            var Q39;
            Q39=makeQuery(id+"F5.opExtrude","CAP_EDGE",EDGE,{"disambiguationData":[OSD([sQuery(id+"F4.wireOp",EDGE,"E6.0.1.0")])],"isStart":false});
            var Q40;
            Q40=makeQuery(id+"F5.opExtrude","CAP_EDGE",EDGE,{"disambiguationData":[OSD([sQuery(id+"F4.wireOp",EDGE,"E6.0.2.4")])],"isStart":false});
            var Q41;
            Q41=makeQuery(id+"F5.opExtrude","CAP_EDGE",EDGE,{"disambiguationData":[OSD([sQuery(id+"F4.wireOp",EDGE,"E6.0.2.2")])],"isStart":false});
            var Q42;
            Q42=makeQuery(id+"F5.opExtrude","CAP_EDGE",EDGE,{"disambiguationData":[OSD([sQuery(id+"F4.wireOp",EDGE,"E6.0.2.0")])],"isStart":false});
            var Q43;
            Q43=makeQuery(id+"F5.opExtrude","CAP_EDGE",EDGE,{"disambiguationData":[OSD([sQuery(id+"F4.wireOp",EDGE,"E6.0.2.6")])],"isStart":false});
            var Q44;
            Q44=makeQuery(id+"F5.opExtrude","CAP_EDGE",EDGE,{"disambiguationData":[OSD([sQuery(id+"F4.wireOp",EDGE,"E6.1.2.4")])],"isStart":false});
            var Q45;
            Q45=makeQuery(id+"F5.opExtrude","CAP_EDGE",EDGE,{"disambiguationData":[OSD([sQuery(id+"F4.wireOp",EDGE,"E6.1.2.0")])],"isStart":false});
            var Q46;
            Q46=makeQuery(id+"F5.opExtrude","CAP_EDGE",EDGE,{"disambiguationData":[OSD([sQuery(id+"F4.wireOp",EDGE,"E6.1.2.2")])],"isStart":false});
            var Q47;
            Q47=makeQuery(id+"F5.opExtrude","CAP_EDGE",EDGE,{"disambiguationData":[OSD([sQuery(id+"F4.wireOp",EDGE,"E6.1.2.6")])],"isStart":false});
            var Q48;
            Q48=makeQuery(id+"F5.opExtrude","CAP_EDGE",EDGE,{"disambiguationData":[OSD([sQuery(id+"F4.wireOp",EDGE,"E6.2.2.2")])],"isStart":false});
            var Q49;
            Q49=makeQuery(id+"F5.opExtrude","CAP_EDGE",EDGE,{"disambiguationData":[OSD([sQuery(id+"F4.wireOp",EDGE,"E6.2.2.4")])],"isStart":false});
            var Q50;
            Q50=makeQuery(id+"F5.opExtrude","CAP_EDGE",EDGE,{"disambiguationData":[OSD([sQuery(id+"F4.wireOp",EDGE,"E6.2.2.6")])],"isStart":false});
            var Q51;
            Q51=makeQuery(id+"F5.opExtrude","CAP_EDGE",EDGE,{"disambiguationData":[OSD([sQuery(id+"F4.wireOp",EDGE,"E6.2.2.0")])],"isStart":false});
            var Q52;
            Q52=makeQuery(id+"F5.opExtrude","CAP_EDGE",EDGE,{"disambiguationData":[OSD([sQuery(id+"F4.wireOp",EDGE,"E6.3.2.2")])],"isStart":false});
            var Q53;
            Q53=makeQuery(id+"F5.opExtrude","CAP_EDGE",EDGE,{"disambiguationData":[OSD([sQuery(id+"F4.wireOp",EDGE,"E6.3.2.4")])],"isStart":false});
            var Q54;
            Q54=makeQuery(id+"F5.opExtrude","CAP_EDGE",EDGE,{"disambiguationData":[OSD([sQuery(id+"F4.wireOp",EDGE,"E6.3.2.6")])],"isStart":false});
            var Q55;
            Q55=makeQuery(id+"F5.opExtrude","CAP_EDGE",EDGE,{"disambiguationData":[OSD([sQuery(id+"F4.wireOp",EDGE,"E6.3.2.0")])],"isStart":false});
            var Q56;
            Q56=makeQuery(id+"F5.opExtrude","CAP_EDGE",EDGE,{"disambiguationData":[OSD([sQuery(id+"F4.wireOp",EDGE,"E6.4.2.4")])],"isStart":false});
            var Q57;
            Q57=makeQuery(id+"F5.opExtrude","CAP_EDGE",EDGE,{"disambiguationData":[OSD([sQuery(id+"F4.wireOp",EDGE,"E6.4.2.2")])],"isStart":false});
            var Q58;
            Q58=makeQuery(id+"F5.opExtrude","CAP_EDGE",EDGE,{"disambiguationData":[OSD([sQuery(id+"F4.wireOp",EDGE,"E6.4.2.6")])],"isStart":false});
            var Q59;
            Q59=makeQuery(id+"F5.opExtrude","CAP_EDGE",EDGE,{"disambiguationData":[OSD([sQuery(id+"F4.wireOp",EDGE,"E6.4.2.0")])],"isStart":false});
            var Q60;
            Q60=makeQuery(id+"F5.opExtrude","CAP_EDGE",EDGE,{"disambiguationData":[OSD([sQuery(id+"F4.wireOp",EDGE,"E6.0.3.4")])],"isStart":false});
            var Q61;
            Q61=makeQuery(id+"F5.opExtrude","CAP_EDGE",EDGE,{"disambiguationData":[OSD([sQuery(id+"F4.wireOp",EDGE,"E6.0.3.2")])],"isStart":false});
            var Q62;
            Q62=makeQuery(id+"F5.opExtrude","CAP_EDGE",EDGE,{"disambiguationData":[OSD([sQuery(id+"F4.wireOp",EDGE,"E6.0.3.6")])],"isStart":false});
            var Q63;
            Q63=makeQuery(id+"F5.opExtrude","CAP_EDGE",EDGE,{"disambiguationData":[OSD([sQuery(id+"F4.wireOp",EDGE,"E6.1.3.2")])],"isStart":false});
            var Q64;
            Q64=makeQuery(id+"F5.opExtrude","CAP_EDGE",EDGE,{"disambiguationData":[OSD([sQuery(id+"F4.wireOp",EDGE,"E6.1.3.4")])],"isStart":false});
            var Q65;
            Q65=makeQuery(id+"F5.opExtrude","CAP_EDGE",EDGE,{"disambiguationData":[OSD([sQuery(id+"F4.wireOp",EDGE,"E6.1.3.6")])],"isStart":false});
            var Q66;
            Q66=makeQuery(id+"F5.opExtrude","CAP_EDGE",EDGE,{"disambiguationData":[OSD([sQuery(id+"F4.wireOp",EDGE,"E6.2.3.2")])],"isStart":false});
            var Q67;
            Q67=makeQuery(id+"F5.opExtrude","CAP_EDGE",EDGE,{"disambiguationData":[OSD([sQuery(id+"F4.wireOp",EDGE,"E6.2.3.4")])],"isStart":false});
            var Q68;
            Q68=makeQuery(id+"F5.opExtrude","CAP_EDGE",EDGE,{"disambiguationData":[OSD([sQuery(id+"F4.wireOp",EDGE,"E6.2.3.6")])],"isStart":false});
            var Q69;
            Q69=makeQuery(id+"F5.opExtrude","CAP_EDGE",EDGE,{"disambiguationData":[OSD([sQuery(id+"F4.wireOp",EDGE,"E6.3.3.2")])],"isStart":false});
            var Q70;
            Q70=makeQuery(id+"F5.opExtrude","CAP_EDGE",EDGE,{"disambiguationData":[OSD([sQuery(id+"F4.wireOp",EDGE,"E6.3.3.4")])],"isStart":false});
            var Q71;
            Q71=makeQuery(id+"F5.opExtrude","CAP_EDGE",EDGE,{"disambiguationData":[OSD([sQuery(id+"F4.wireOp",EDGE,"E6.3.3.6")])],"isStart":false});
            var Q72;
            Q72=makeQuery(id+"F5.opExtrude","CAP_EDGE",EDGE,{"disambiguationData":[OSD([sQuery(id+"F4.wireOp",EDGE,"E6.4.3.2")])],"isStart":false});
            var Q73;
            Q73=makeQuery(id+"F5.opExtrude","CAP_EDGE",EDGE,{"disambiguationData":[OSD([sQuery(id+"F4.wireOp",EDGE,"E6.4.3.4")])],"isStart":false});
            var Q74;
            Q74=makeQuery(id+"F5.opExtrude","CAP_EDGE",EDGE,{"disambiguationData":[OSD([sQuery(id+"F4.wireOp",EDGE,"E6.4.3.6")])],"isStart":false});
            var Q75;
            Q75=makeQuery(id+"F5.opExtrude","CAP_EDGE",EDGE,{"disambiguationData":[OSD([sQuery(id+"F4.wireOp",EDGE,"E6.0.3.0")])],"isStart":false});
            var Q76;
            Q76=makeQuery(id+"F5.opExtrude","CAP_EDGE",EDGE,{"disambiguationData":[OSD([sQuery(id+"F4.wireOp",EDGE,"E6.1.3.0")])],"isStart":false});
            var Q77;
            Q77=makeQuery(id+"F5.opExtrude","CAP_EDGE",EDGE,{"disambiguationData":[OSD([sQuery(id+"F4.wireOp",EDGE,"E6.2.3.0")])],"isStart":false});
            var Q78;
            Q78=makeQuery(id+"F5.opExtrude","CAP_EDGE",EDGE,{"disambiguationData":[OSD([sQuery(id+"F4.wireOp",EDGE,"E6.3.3.0")])],"isStart":false});
            var Q79;
            Q79=makeQuery(id+"F5.opExtrude","CAP_EDGE",EDGE,{"disambiguationData":[OSD([sQuery(id+"F4.wireOp",EDGE,"E6.4.3.0")])],"isStart":false});
            var Q80;
            Q80=makeQuery(id+"F5.opExtrude","CAP_EDGE",EDGE,{"disambiguationData":[OSD([sQuery(id+"F4.wireOp",EDGE,"E6.4.4.4")])],"isStart":false});
            var Q81;
            Q81=makeQuery(id+"F5.opExtrude","CAP_EDGE",EDGE,{"disambiguationData":[OSD([sQuery(id+"F4.wireOp",EDGE,"E6.4.4.6")])],"isStart":false});
            var Q82;
            Q82=makeQuery(id+"F5.opExtrude","CAP_EDGE",EDGE,{"disambiguationData":[OSD([sQuery(id+"F4.wireOp",EDGE,"E6.4.4.0")])],"isStart":false});
            var Q83;
            Q83=makeQuery(id+"F5.opExtrude","CAP_EDGE",EDGE,{"disambiguationData":[OSD([sQuery(id+"F4.wireOp",EDGE,"E6.4.4.2")])],"isStart":false});
            var Q84;
            Q84=makeQuery(id+"F5.opExtrude","CAP_EDGE",EDGE,{"disambiguationData":[OSD([sQuery(id+"F4.wireOp",EDGE,"E6.3.4.6")])],"isStart":false});
            var Q85;
            Q85=makeQuery(id+"F5.opExtrude","CAP_EDGE",EDGE,{"disambiguationData":[OSD([sQuery(id+"F4.wireOp",EDGE,"E6.3.4.4")])],"isStart":false});
            var Q86;
            Q86=makeQuery(id+"F5.opExtrude","CAP_EDGE",EDGE,{"disambiguationData":[OSD([sQuery(id+"F4.wireOp",EDGE,"E6.3.4.2")])],"isStart":false});
            var Q87;
            Q87=makeQuery(id+"F5.opExtrude","CAP_EDGE",EDGE,{"disambiguationData":[OSD([sQuery(id+"F4.wireOp",EDGE,"E6.3.4.0")])],"isStart":false});
            var Q88;
            Q88=makeQuery(id+"F5.opExtrude","CAP_EDGE",EDGE,{"disambiguationData":[OSD([sQuery(id+"F4.wireOp",EDGE,"E6.2.4.6")])],"isStart":false});
            var Q89;
            Q89=makeQuery(id+"F5.opExtrude","CAP_EDGE",EDGE,{"disambiguationData":[OSD([sQuery(id+"F4.wireOp",EDGE,"E6.2.4.4")])],"isStart":false});
            var Q90;
            Q90=makeQuery(id+"F5.opExtrude","CAP_EDGE",EDGE,{"disambiguationData":[OSD([sQuery(id+"F4.wireOp",EDGE,"E6.2.4.0")])],"isStart":false});
            var Q91;
            Q91=makeQuery(id+"F5.opExtrude","CAP_EDGE",EDGE,{"disambiguationData":[OSD([sQuery(id+"F4.wireOp",EDGE,"E6.2.4.2")])],"isStart":false});
            var Q92;
            Q92=makeQuery(id+"F5.opExtrude","CAP_EDGE",EDGE,{"disambiguationData":[OSD([sQuery(id+"F4.wireOp",EDGE,"E6.1.4.6")])],"isStart":false});
            var Q93;
            Q93=makeQuery(id+"F5.opExtrude","CAP_EDGE",EDGE,{"disambiguationData":[OSD([sQuery(id+"F4.wireOp",EDGE,"E6.1.4.4")])],"isStart":false});
            var Q94;
            Q94=makeQuery(id+"F5.opExtrude","CAP_EDGE",EDGE,{"disambiguationData":[OSD([sQuery(id+"F4.wireOp",EDGE,"E6.1.4.2")])],"isStart":false});
            var Q95;
            Q95=makeQuery(id+"F5.opExtrude","CAP_EDGE",EDGE,{"disambiguationData":[OSD([sQuery(id+"F4.wireOp",EDGE,"E6.1.4.0")])],"isStart":false});
            var Q96;
            Q96=makeQuery(id+"F5.opExtrude","CAP_EDGE",EDGE,{"disambiguationData":[OSD([sQuery(id+"F4.wireOp",EDGE,"E6.0.4.6")])],"isStart":false});
            var Q97;
            Q97=makeQuery(id+"F5.opExtrude","CAP_EDGE",EDGE,{"disambiguationData":[OSD([sQuery(id+"F4.wireOp",EDGE,"E6.0.4.4")])],"isStart":false});
            var Q98;
            Q98=makeQuery(id+"F5.opExtrude","CAP_EDGE",EDGE,{"disambiguationData":[OSD([sQuery(id+"F4.wireOp",EDGE,"E6.0.4.2")])],"isStart":false});
            var Q99;
            Q99=makeQuery(id+"F5.opExtrude","CAP_EDGE",EDGE,{"disambiguationData":[OSD([sQuery(id+"F4.wireOp",EDGE,"E6.0.4.0")])],"isStart":false});
            var Q100;
            Q100=makeQuery(id+"F5.opExtrude","CAP_EDGE",EDGE,{"disambiguationData":[OSD([sQuery(id+"F4.wireOp",EDGE,"E2")])],"isStart":false});
            var Q101;
            Q101=makeQuery(id+"F5.opExtrude","CAP_EDGE",EDGE,{"disambiguationData":[OSD([sQuery(id+"F4.wireOp",EDGE,"E3")])],"isStart":false});
            var Q102;
            Q102=makeQuery(id+"F5.opExtrude","CAP_EDGE",EDGE,{"disambiguationData":[OSD([sQuery(id+"F4.wireOp",EDGE,"E4")])],"isStart":false});
            var Q103;
            Q103=makeQuery(id+"F5.opExtrude","CAP_EDGE",EDGE,{"disambiguationData":[OSD([sQuery(id+"F4.wireOp",EDGE,"E5")])],"isStart":false});
            var Q104;
            Q104=makeQuery(id+"F5.opExtrude","CAP_EDGE",EDGE,{"disambiguationData":[OSD([sQuery(id+"F4.wireOp",EDGE,"E6.1.0.1")])],"isStart":false});
            var Q105;
            Q105=makeQuery(id+"F5.opExtrude","CAP_EDGE",EDGE,{"disambiguationData":[OSD([sQuery(id+"F4.wireOp",EDGE,"E6.1.0.3")])],"isStart":false});
            var Q106;
            Q106=makeQuery(id+"F5.opExtrude","CAP_EDGE",EDGE,{"disambiguationData":[OSD([sQuery(id+"F4.wireOp",EDGE,"E6.1.0.5")])],"isStart":false});
            var Q107;
            Q107=makeQuery(id+"F5.opExtrude","CAP_EDGE",EDGE,{"disambiguationData":[OSD([sQuery(id+"F4.wireOp",EDGE,"E6.1.0.7")])],"isStart":false});
            var Q108;
            Q108=makeQuery(id+"F5.opExtrude","CAP_EDGE",EDGE,{"disambiguationData":[OSD([sQuery(id+"F4.wireOp",EDGE,"E6.2.0.1")])],"isStart":false});
            var Q109;
            Q109=makeQuery(id+"F5.opExtrude","CAP_EDGE",EDGE,{"disambiguationData":[OSD([sQuery(id+"F4.wireOp",EDGE,"E6.2.0.3")])],"isStart":false});
            var Q110;
            Q110=makeQuery(id+"F5.opExtrude","CAP_EDGE",EDGE,{"disambiguationData":[OSD([sQuery(id+"F4.wireOp",EDGE,"E6.2.0.5")])],"isStart":false});
            var Q111;
            Q111=makeQuery(id+"F5.opExtrude","CAP_EDGE",EDGE,{"disambiguationData":[OSD([sQuery(id+"F4.wireOp",EDGE,"E6.2.0.7")])],"isStart":false});
            var Q112;
            Q112=makeQuery(id+"F5.opExtrude","CAP_EDGE",EDGE,{"disambiguationData":[OSD([sQuery(id+"F4.wireOp",EDGE,"E6.3.0.3")])],"isStart":false});
            var Q113;
            Q113=makeQuery(id+"F5.opExtrude","CAP_EDGE",EDGE,{"disambiguationData":[OSD([sQuery(id+"F4.wireOp",EDGE,"E6.3.0.1")])],"isStart":false});
            var Q114;
            Q114=makeQuery(id+"F5.opExtrude","CAP_EDGE",EDGE,{"disambiguationData":[OSD([sQuery(id+"F4.wireOp",EDGE,"E6.3.0.7")])],"isStart":false});
            var Q115;
            Q115=makeQuery(id+"F5.opExtrude","CAP_EDGE",EDGE,{"disambiguationData":[OSD([sQuery(id+"F4.wireOp",EDGE,"E6.3.0.5")])],"isStart":false});
            var Q116;
            Q116=makeQuery(id+"F5.opExtrude","CAP_EDGE",EDGE,{"disambiguationData":[OSD([sQuery(id+"F4.wireOp",EDGE,"E6.4.0.3")])],"isStart":false});
            var Q117;
            Q117=makeQuery(id+"F5.opExtrude","CAP_EDGE",EDGE,{"disambiguationData":[OSD([sQuery(id+"F4.wireOp",EDGE,"E6.4.0.5")])],"isStart":false});
            var Q118;
            Q118=makeQuery(id+"F5.opExtrude","CAP_EDGE",EDGE,{"disambiguationData":[OSD([sQuery(id+"F4.wireOp",EDGE,"E6.4.0.7")])],"isStart":false});
            var Q119;
            Q119=makeQuery(id+"F5.opExtrude","CAP_EDGE",EDGE,{"disambiguationData":[OSD([sQuery(id+"F4.wireOp",EDGE,"E6.4.0.1")])],"isStart":false});
            var Q120;
            Q120=makeQuery(id+"F5.opExtrude","CAP_EDGE",EDGE,{"disambiguationData":[OSD([sQuery(id+"F4.wireOp",EDGE,"E6.0.1.3")])],"isStart":false});
            var Q121;
            Q121=makeQuery(id+"F5.opExtrude","CAP_EDGE",EDGE,{"disambiguationData":[OSD([sQuery(id+"F4.wireOp",EDGE,"E6.0.1.1")])],"isStart":false});
            var Q122;
            Q122=makeQuery(id+"F5.opExtrude","CAP_EDGE",EDGE,{"disambiguationData":[OSD([sQuery(id+"F4.wireOp",EDGE,"E6.0.1.7")])],"isStart":false});
            var Q123;
            Q123=makeQuery(id+"F5.opExtrude","CAP_EDGE",EDGE,{"disambiguationData":[OSD([sQuery(id+"F4.wireOp",EDGE,"E6.0.1.5")])],"isStart":false});
            var Q124;
            Q124=makeQuery(id+"F5.opExtrude","CAP_EDGE",EDGE,{"disambiguationData":[OSD([sQuery(id+"F4.wireOp",EDGE,"E6.1.1.3")])],"isStart":false});
            var Q125;
            Q125=makeQuery(id+"F5.opExtrude","CAP_EDGE",EDGE,{"disambiguationData":[OSD([sQuery(id+"F4.wireOp",EDGE,"E6.1.1.5")])],"isStart":false});
            var Q126;
            Q126=makeQuery(id+"F5.opExtrude","CAP_EDGE",EDGE,{"disambiguationData":[OSD([sQuery(id+"F4.wireOp",EDGE,"E6.1.1.7")])],"isStart":false});
            var Q127;
            Q127=makeQuery(id+"F5.opExtrude","CAP_EDGE",EDGE,{"disambiguationData":[OSD([sQuery(id+"F4.wireOp",EDGE,"E6.1.1.1")])],"isStart":false});
            var Q128;
            Q128=makeQuery(id+"F5.opExtrude","CAP_EDGE",EDGE,{"disambiguationData":[OSD([sQuery(id+"F4.wireOp",EDGE,"E6.2.1.1")])],"isStart":false});
            var Q129;
            Q129=makeQuery(id+"F5.opExtrude","CAP_EDGE",EDGE,{"disambiguationData":[OSD([sQuery(id+"F4.wireOp",EDGE,"E6.2.1.3")])],"isStart":false});
            var Q130;
            Q130=makeQuery(id+"F5.opExtrude","CAP_EDGE",EDGE,{"disambiguationData":[OSD([sQuery(id+"F4.wireOp",EDGE,"E6.2.1.5")])],"isStart":false});
            var Q131;
            Q131=makeQuery(id+"F5.opExtrude","CAP_EDGE",EDGE,{"disambiguationData":[OSD([sQuery(id+"F4.wireOp",EDGE,"E6.2.1.7")])],"isStart":false});
            var Q132;
            Q132=makeQuery(id+"F5.opExtrude","CAP_EDGE",EDGE,{"disambiguationData":[OSD([sQuery(id+"F4.wireOp",EDGE,"E6.3.1.3")])],"isStart":false});
            var Q133;
            Q133=makeQuery(id+"F5.opExtrude","CAP_EDGE",EDGE,{"disambiguationData":[OSD([sQuery(id+"F4.wireOp",EDGE,"E6.3.1.5")])],"isStart":false});
            var Q134;
            Q134=makeQuery(id+"F5.opExtrude","CAP_EDGE",EDGE,{"disambiguationData":[OSD([sQuery(id+"F4.wireOp",EDGE,"E6.4.1.3")])],"isStart":false});
            var Q135;
            Q135=makeQuery(id+"F5.opExtrude","CAP_EDGE",EDGE,{"disambiguationData":[OSD([sQuery(id+"F4.wireOp",EDGE,"E6.4.1.5")])],"isStart":false});
            var Q136;
            Q136=makeQuery(id+"F5.opExtrude","CAP_EDGE",EDGE,{"disambiguationData":[OSD([sQuery(id+"F4.wireOp",EDGE,"E6.4.1.7")])],"isStart":false});
            var Q137;
            Q137=makeQuery(id+"F5.opExtrude","CAP_EDGE",EDGE,{"disambiguationData":[OSD([sQuery(id+"F4.wireOp",EDGE,"E6.4.1.1")])],"isStart":false});
            var Q138;
            Q138=makeQuery(id+"F5.opExtrude","CAP_EDGE",EDGE,{"disambiguationData":[OSD([sQuery(id+"F4.wireOp",EDGE,"E6.3.1.7")])],"isStart":false});
            var Q139;
            Q139=makeQuery(id+"F5.opExtrude","CAP_EDGE",EDGE,{"disambiguationData":[OSD([sQuery(id+"F4.wireOp",EDGE,"E6.3.1.1")])],"isStart":false});
            var Q140;
            Q140=makeQuery(id+"F5.opExtrude","CAP_EDGE",EDGE,{"disambiguationData":[OSD([sQuery(id+"F4.wireOp",EDGE,"E6.0.2.3")])],"isStart":false});
            var Q141;
            Q141=makeQuery(id+"F5.opExtrude","CAP_EDGE",EDGE,{"disambiguationData":[OSD([sQuery(id+"F4.wireOp",EDGE,"E6.0.2.5")])],"isStart":false});
            var Q142;
            Q142=makeQuery(id+"F5.opExtrude","CAP_EDGE",EDGE,{"disambiguationData":[OSD([sQuery(id+"F4.wireOp",EDGE,"E6.1.2.3")])],"isStart":false});
            var Q143;
            Q143=makeQuery(id+"F5.opExtrude","CAP_EDGE",EDGE,{"disambiguationData":[OSD([sQuery(id+"F4.wireOp",EDGE,"E6.1.2.5")])],"isStart":false});
            var Q144;
            Q144=makeQuery(id+"F5.opExtrude","CAP_EDGE",EDGE,{"disambiguationData":[OSD([sQuery(id+"F4.wireOp",EDGE,"E6.2.2.3")])],"isStart":false});
            var Q145;
            Q145=makeQuery(id+"F5.opExtrude","CAP_EDGE",EDGE,{"disambiguationData":[OSD([sQuery(id+"F4.wireOp",EDGE,"E6.2.2.5")])],"isStart":false});
            var Q146;
            Q146=makeQuery(id+"F5.opExtrude","CAP_EDGE",EDGE,{"disambiguationData":[OSD([sQuery(id+"F4.wireOp",EDGE,"E6.3.2.3")])],"isStart":false});
            var Q147;
            Q147=makeQuery(id+"F5.opExtrude","CAP_EDGE",EDGE,{"disambiguationData":[OSD([sQuery(id+"F4.wireOp",EDGE,"E6.3.2.5")])],"isStart":false});
            var Q148;
            Q148=makeQuery(id+"F5.opExtrude","CAP_EDGE",EDGE,{"disambiguationData":[OSD([sQuery(id+"F4.wireOp",EDGE,"E6.4.2.3")])],"isStart":false});
            var Q149;
            Q149=makeQuery(id+"F5.opExtrude","CAP_EDGE",EDGE,{"disambiguationData":[OSD([sQuery(id+"F4.wireOp",EDGE,"E6.4.2.5")])],"isStart":false});
            var Q150;
            Q150=makeQuery(id+"F5.opExtrude","CAP_EDGE",EDGE,{"disambiguationData":[OSD([sQuery(id+"F4.wireOp",EDGE,"E6.4.2.7")])],"isStart":false});
            var Q151;
            Q151=makeQuery(id+"F5.opExtrude","CAP_EDGE",EDGE,{"disambiguationData":[OSD([sQuery(id+"F4.wireOp",EDGE,"E6.4.2.1")])],"isStart":false});
            var Q152;
            Q152=makeQuery(id+"F5.opExtrude","CAP_EDGE",EDGE,{"disambiguationData":[OSD([sQuery(id+"F4.wireOp",EDGE,"E6.3.2.7")])],"isStart":false});
            var Q153;
            Q153=makeQuery(id+"F5.opExtrude","CAP_EDGE",EDGE,{"disambiguationData":[OSD([sQuery(id+"F4.wireOp",EDGE,"E6.3.2.1")])],"isStart":false});
            var Q154;
            Q154=makeQuery(id+"F5.opExtrude","CAP_EDGE",EDGE,{"disambiguationData":[OSD([sQuery(id+"F4.wireOp",EDGE,"E6.2.2.7")])],"isStart":false});
            var Q155;
            Q155=makeQuery(id+"F5.opExtrude","CAP_EDGE",EDGE,{"disambiguationData":[OSD([sQuery(id+"F4.wireOp",EDGE,"E6.2.2.1")])],"isStart":false});
            var Q156;
            Q156=makeQuery(id+"F5.opExtrude","CAP_EDGE",EDGE,{"disambiguationData":[OSD([sQuery(id+"F4.wireOp",EDGE,"E6.1.2.7")])],"isStart":false});
            var Q157;
            Q157=makeQuery(id+"F5.opExtrude","CAP_EDGE",EDGE,{"disambiguationData":[OSD([sQuery(id+"F4.wireOp",EDGE,"E6.1.2.1")])],"isStart":false});
            var Q158;
            Q158=makeQuery(id+"F5.opExtrude","CAP_EDGE",EDGE,{"disambiguationData":[OSD([sQuery(id+"F4.wireOp",EDGE,"E6.0.2.7")])],"isStart":false});
            var Q159;
            Q159=makeQuery(id+"F5.opExtrude","CAP_EDGE",EDGE,{"disambiguationData":[OSD([sQuery(id+"F4.wireOp",EDGE,"E6.0.2.1")])],"isStart":false});
            var Q160;
            Q160=makeQuery(id+"F5.opExtrude","CAP_EDGE",EDGE,{"disambiguationData":[OSD([sQuery(id+"F4.wireOp",EDGE,"E6.0.3.3")])],"isStart":false});
            var Q161;
            Q161=makeQuery(id+"F5.opExtrude","CAP_EDGE",EDGE,{"disambiguationData":[OSD([sQuery(id+"F4.wireOp",EDGE,"E6.0.3.5")])],"isStart":false});
            var Q162;
            Q162=makeQuery(id+"F5.opExtrude","CAP_EDGE",EDGE,{"disambiguationData":[OSD([sQuery(id+"F4.wireOp",EDGE,"E6.1.3.3")])],"isStart":false});
            var Q163;
            Q163=makeQuery(id+"F5.opExtrude","CAP_EDGE",EDGE,{"disambiguationData":[OSD([sQuery(id+"F4.wireOp",EDGE,"E6.1.3.5")])],"isStart":false});
            var Q164;
            Q164=makeQuery(id+"F5.opExtrude","CAP_EDGE",EDGE,{"disambiguationData":[OSD([sQuery(id+"F4.wireOp",EDGE,"E6.2.3.3")])],"isStart":false});
            var Q165;
            Q165=makeQuery(id+"F5.opExtrude","CAP_EDGE",EDGE,{"disambiguationData":[OSD([sQuery(id+"F4.wireOp",EDGE,"E6.2.3.5")])],"isStart":false});
            var Q166;
            Q166=makeQuery(id+"F5.opExtrude","CAP_EDGE",EDGE,{"disambiguationData":[OSD([sQuery(id+"F4.wireOp",EDGE,"E6.3.3.3")])],"isStart":false});
            var Q167;
            Q167=makeQuery(id+"F5.opExtrude","CAP_EDGE",EDGE,{"disambiguationData":[OSD([sQuery(id+"F4.wireOp",EDGE,"E6.3.3.5")])],"isStart":false});
            var Q168;
            Q168=makeQuery(id+"F5.opExtrude","CAP_EDGE",EDGE,{"disambiguationData":[OSD([sQuery(id+"F4.wireOp",EDGE,"E6.4.3.3")])],"isStart":false});
            var Q169;
            Q169=makeQuery(id+"F5.opExtrude","CAP_EDGE",EDGE,{"disambiguationData":[OSD([sQuery(id+"F4.wireOp",EDGE,"E6.4.3.5")])],"isStart":false});
            var Q170;
            Q170=makeQuery(id+"F5.opExtrude","CAP_EDGE",EDGE,{"disambiguationData":[OSD([sQuery(id+"F4.wireOp",EDGE,"E6.4.3.7")])],"isStart":false});
            var Q171;
            Q171=makeQuery(id+"F5.opExtrude","CAP_EDGE",EDGE,{"disambiguationData":[OSD([sQuery(id+"F4.wireOp",EDGE,"E6.4.3.1")])],"isStart":false});
            var Q172;
            Q172=makeQuery(id+"F5.opExtrude","CAP_EDGE",EDGE,{"disambiguationData":[OSD([sQuery(id+"F4.wireOp",EDGE,"E6.3.3.7")])],"isStart":false});
            var Q173;
            Q173=makeQuery(id+"F5.opExtrude","CAP_EDGE",EDGE,{"disambiguationData":[OSD([sQuery(id+"F4.wireOp",EDGE,"E6.3.3.1")])],"isStart":false});
            var Q174;
            Q174=makeQuery(id+"F5.opExtrude","CAP_EDGE",EDGE,{"disambiguationData":[OSD([sQuery(id+"F4.wireOp",EDGE,"E6.2.3.7")])],"isStart":false});
            var Q175;
            Q175=makeQuery(id+"F5.opExtrude","CAP_EDGE",EDGE,{"disambiguationData":[OSD([sQuery(id+"F4.wireOp",EDGE,"E6.2.3.1")])],"isStart":false});
            var Q176;
            Q176=makeQuery(id+"F5.opExtrude","CAP_EDGE",EDGE,{"disambiguationData":[OSD([sQuery(id+"F4.wireOp",EDGE,"E6.1.3.7")])],"isStart":false});
            var Q177;
            Q177=makeQuery(id+"F5.opExtrude","CAP_EDGE",EDGE,{"disambiguationData":[OSD([sQuery(id+"F4.wireOp",EDGE,"E6.1.3.1")])],"isStart":false});
            var Q178;
            Q178=makeQuery(id+"F5.opExtrude","CAP_EDGE",EDGE,{"disambiguationData":[OSD([sQuery(id+"F4.wireOp",EDGE,"E6.0.3.7")])],"isStart":false});
            var Q179;
            Q179=makeQuery(id+"F5.opExtrude","CAP_EDGE",EDGE,{"disambiguationData":[OSD([sQuery(id+"F4.wireOp",EDGE,"E6.0.3.1")])],"isStart":false});
            var Q180;
            Q180=makeQuery(id+"F5.opExtrude","CAP_EDGE",EDGE,{"disambiguationData":[OSD([sQuery(id+"F4.wireOp",EDGE,"E6.0.4.3")])],"isStart":false});
            var Q181;
            Q181=makeQuery(id+"F5.opExtrude","CAP_EDGE",EDGE,{"disambiguationData":[OSD([sQuery(id+"F4.wireOp",EDGE,"E6.0.4.5")])],"isStart":false});
            var Q182;
            Q182=makeQuery(id+"F5.opExtrude","CAP_EDGE",EDGE,{"disambiguationData":[OSD([sQuery(id+"F4.wireOp",EDGE,"E6.1.4.3")])],"isStart":false});
            var Q183;
            Q183=makeQuery(id+"F5.opExtrude","CAP_EDGE",EDGE,{"disambiguationData":[OSD([sQuery(id+"F4.wireOp",EDGE,"E6.1.4.5")])],"isStart":false});
            var Q184;
            Q184=makeQuery(id+"F5.opExtrude","CAP_EDGE",EDGE,{"disambiguationData":[OSD([sQuery(id+"F4.wireOp",EDGE,"E6.2.4.3")])],"isStart":false});
            var Q185;
            Q185=makeQuery(id+"F5.opExtrude","CAP_EDGE",EDGE,{"disambiguationData":[OSD([sQuery(id+"F4.wireOp",EDGE,"E6.2.4.5")])],"isStart":false});
            var Q186;
            Q186=makeQuery(id+"F5.opExtrude","CAP_EDGE",EDGE,{"disambiguationData":[OSD([sQuery(id+"F4.wireOp",EDGE,"E6.3.4.3")])],"isStart":false});
            var Q187;
            Q187=makeQuery(id+"F5.opExtrude","CAP_EDGE",EDGE,{"disambiguationData":[OSD([sQuery(id+"F4.wireOp",EDGE,"E6.3.4.5")])],"isStart":false});
            var Q188;
            Q188=makeQuery(id+"F5.opExtrude","CAP_EDGE",EDGE,{"disambiguationData":[OSD([sQuery(id+"F4.wireOp",EDGE,"E6.4.4.3")])],"isStart":false});
            var Q189;
            Q189=makeQuery(id+"F5.opExtrude","CAP_EDGE",EDGE,{"disambiguationData":[OSD([sQuery(id+"F4.wireOp",EDGE,"E6.4.4.5")])],"isStart":false});
            var Q190;
            Q190=makeQuery(id+"F5.opExtrude","CAP_EDGE",EDGE,{"disambiguationData":[OSD([sQuery(id+"F4.wireOp",EDGE,"E6.4.4.7")])],"isStart":false});
            var Q191;
            Q191=makeQuery(id+"F5.opExtrude","CAP_EDGE",EDGE,{"disambiguationData":[OSD([sQuery(id+"F4.wireOp",EDGE,"E6.4.4.1")])],"isStart":false});
            var Q192;
            Q192=makeQuery(id+"F5.opExtrude","CAP_EDGE",EDGE,{"disambiguationData":[OSD([sQuery(id+"F4.wireOp",EDGE,"E6.3.4.7")])],"isStart":false});
            var Q193;
            Q193=makeQuery(id+"F5.opExtrude","CAP_EDGE",EDGE,{"disambiguationData":[OSD([sQuery(id+"F4.wireOp",EDGE,"E6.3.4.1")])],"isStart":false});
            var Q194;
            Q194=makeQuery(id+"F5.opExtrude","CAP_EDGE",EDGE,{"disambiguationData":[OSD([sQuery(id+"F4.wireOp",EDGE,"E6.2.4.7")])],"isStart":false});
            var Q195;
            Q195=makeQuery(id+"F5.opExtrude","CAP_EDGE",EDGE,{"disambiguationData":[OSD([sQuery(id+"F4.wireOp",EDGE,"E6.2.4.1")])],"isStart":false});
            var Q196;
            Q196=makeQuery(id+"F5.opExtrude","CAP_EDGE",EDGE,{"disambiguationData":[OSD([sQuery(id+"F4.wireOp",EDGE,"E6.1.4.7")])],"isStart":false});
            var Q197;
            Q197=makeQuery(id+"F5.opExtrude","CAP_EDGE",EDGE,{"disambiguationData":[OSD([sQuery(id+"F4.wireOp",EDGE,"E6.1.4.1")])],"isStart":false});
            var Q198;
            Q198=makeQuery(id+"F5.opExtrude","CAP_EDGE",EDGE,{"disambiguationData":[OSD([sQuery(id+"F4.wireOp",EDGE,"E6.0.4.7")])],"isStart":false});
            var Q199;
            Q199=makeQuery(id+"F5.opExtrude","CAP_EDGE",EDGE,{"disambiguationData":[OSD([sQuery(id+"F4.wireOp",EDGE,"E6.0.4.1")])],"isStart":false});
            chamfer(context, id + "F8", {"entities" : qUnion([Q0, Q1, Q2, Q3, Q4, Q5, Q6, Q7, Q8, Q9, Q10, Q11, Q12, Q13, Q14, Q15, Q16, Q17, Q18, Q19, Q20, Q21, Q22, Q23, Q24, Q25, Q26, Q27, Q28, Q29, Q30, Q31, Q32, Q33, Q34, Q35, Q36, Q37, Q38, Q39, Q40, Q41, Q42, Q43, Q44, Q45, Q46, Q47, Q48, Q49, Q50, Q51, Q52, Q53, Q54, Q55, Q56, Q57, Q58, Q59, Q60, Q61, Q62, Q63, Q64, Q65, Q66, Q67, Q68, Q69, Q70, Q71, Q72, Q73, Q74, Q75, Q76, Q77, Q78, Q79, Q80, Q81, Q82, Q83, Q84, Q85, Q86, Q87, Q88, Q89, Q90, Q91, Q92, Q93, Q94, Q95, Q96, Q97, Q98, Q99, Q100, Q101, Q102, Q103, Q104, Q105, Q106, Q107, Q108, Q109, Q110, Q111, Q112, Q113, Q114, Q115, Q116, Q117, Q118, Q119, Q120, Q121, Q122, Q123, Q124, Q125, Q126, Q127, Q128, Q129, Q130, Q131, Q132, Q133, Q134, Q135, Q136, Q137, Q138, Q139, Q140, Q141, Q142, Q143, Q144, Q145, Q146, Q147, Q148, Q149, Q150, Q151, Q152, Q153, Q154, Q155, Q156, Q157, Q158, Q159, Q160, Q161, Q162, Q163, Q164, Q165, Q166, Q167, Q168, Q169, Q170, Q171, Q172, Q173, Q174, Q175, Q176, Q177, Q178, Q179, Q180, Q181, Q182, Q183, Q184, Q185, Q186, Q187, Q188, Q189, Q190, Q191, Q192, Q193, Q194, Q195, Q196, Q197, Q198, Q199]), "chamferType" : ChamferType.OFFSET_ANGLE, "width" : .5 * mm, "oppositeDirection" : false, "angle" : 75 * degree, "tangentPropagation" : true});
        }
        {
            var Q0;
            Q0=makeQuery(id+"F5.opExtrude","CAP_EDGE",EDGE,{"disambiguationData":[OSD([sQuery(id+"F0.wireOp",EDGE,"E0.left")])],"isStart":false});
            var Q1;
            Q1=makeQuery(id+"F5.opExtrude","CAP_EDGE",EDGE,{"disambiguationData":[OSD([sQuery(id+"F0.wireOp",EDGE,"E0.bottom")])],"isStart":false});
            var Q2;
            Q2=makeQuery(id+"F5.opExtrude","CAP_EDGE",EDGE,{"disambiguationData":[OSD([sQuery(id+"F0.wireOp",EDGE,"E0.right")])],"isStart":false});
            var Q3;
            {var subQ0=sQuery(id+"F0.wireOp",EDGE,"E0.right");var subQ1=sQuery(id+"F0.wireOp",EDGE,"E0.left");var subQ2=sQuery(id+"F0.wireOp",EDGE,"E0.top");var subQ3=sQuery(id+"F0.wireOp",EDGE,"E0.bottom");Q3=makeQuery(id+"F5.opExtrude","CAP_EDGE",EDGE,{"disambiguationData":[OSD([subQ3,subQ2,subQ1,subQ0]),TDD([makeQuery(id+"F4.imprint","IMPRINT",EDGE,{"derivedFrom":makeQuery(id+"F3.opFillet","BLEND_EDGE",EDGE,{"blendedFrom":[makeQuery(id+"F1.opExtrude","SWEPT_EDGE",EDGE,{"disambiguationData":[OSD([subQ3,subQ0])]}),makeQuery(id+"F1.opExtrude","CAP_FACE",FACE,{"disambiguationData":[OSD([subQ3,subQ2,subQ1,subQ0])],"isStart":false})],"blendedInto":[makeQuery(id+"F1.opExtrude","CAP_FACE",FACE,{"disambiguationData":[OSD([subQ3,subQ2,subQ1,subQ0])],"isStart":false})]})})])],"isStart":false});}
            var Q4;
            {var subQ0=sQuery(id+"F0.wireOp",EDGE,"E0.right");var subQ1=sQuery(id+"F0.wireOp",EDGE,"E0.left");var subQ2=sQuery(id+"F0.wireOp",EDGE,"E0.top");var subQ3=sQuery(id+"F0.wireOp",EDGE,"E0.bottom");Q4=makeQuery(id+"F5.opExtrude","CAP_EDGE",EDGE,{"disambiguationData":[OSD([subQ3,subQ2,subQ1,subQ0]),TDD([makeQuery(id+"F4.imprint","IMPRINT",EDGE,{"derivedFrom":makeQuery(id+"F2.opChamfer","BLEND_EDGE",EDGE,{"blendedFrom":[makeQuery(id+"F1.opExtrude","SWEPT_EDGE",EDGE,{"disambiguationData":[OSD([subQ3,subQ1])]}),makeQuery(id+"F1.opExtrude","CAP_FACE",FACE,{"disambiguationData":[OSD([subQ3,subQ2,subQ1,subQ0])],"isStart":false})],"blendedInto":[makeQuery(id+"F1.opExtrude","CAP_FACE",FACE,{"disambiguationData":[OSD([subQ3,subQ2,subQ1,subQ0])],"isStart":false})]})})])],"isStart":false});}
            chamfer(context, id + "F9", {"entities" : qUnion([Q0, Q1, Q2, Q3, Q4]), "chamferType" : ChamferType.OFFSET_ANGLE, "width" : 2 * mm, "oppositeDirection" : false, "angle" : 45 * degree, "tangentPropagation" : true});
        }
    });
